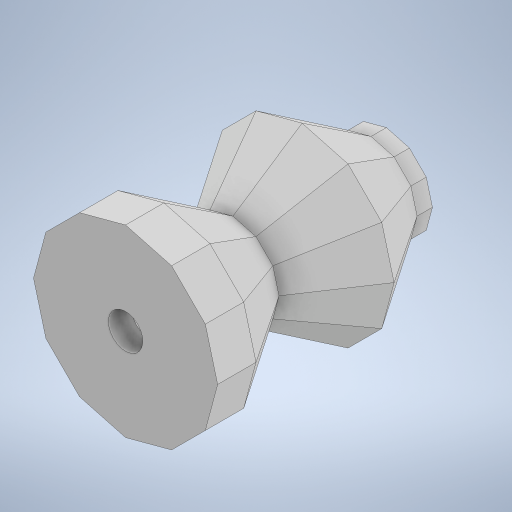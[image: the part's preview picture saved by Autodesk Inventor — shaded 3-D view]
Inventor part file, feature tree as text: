
AUTODESK INVENTOR PART (.ipt)
format: ipt  version: 2023 (Build 270158000, 158)  size: 359,424 bytes
history: native  units: in
note: dims shown in document units (in); Inventor stores cm internally (conversion verified against a paired STEP export)
features: sketch x6, extrude x4, projected_geometry x3, other x2, mirror x2, loft x1, shell x1
ambient origin geometry x8: Origin, YZ Plane, XZ Plane, XY Plane, X Axis, Y Axis, Z Axis, Center Point
bodies: Body1 (feature_tree)
feature tree (19):
  other  "솔리드1"
  sketch  "스케치1"
  other  "작업 평면1"
  loft  "로프트1"
  mirror  "미러1"
  mirror  "미러2"
  extrude  "돌출1"  Depth=0.3543in
  shell  "쉘5"  Thickness=0.4724in
  extrude  "돌출14"  TaperAngle=0.0deg  [1 undecoded]
  extrude  "돌출15"  TaperAngle=0.0deg  [1 undecoded]
  extrude  "돌출16"  Depth=0.1299in TaperAngle=0.0deg
  sketch  "스케치2"
  sketch  "스케치3"
  projected_geometry  "투영된 루프1"
  sketch  "스케치16"
  projected_geometry  "투영된 루프10"
  sketch  "스케치17"
  sketch  "스케치18"
  projected_geometry  "투영된 루프11"
note: 2 required parameter values undecoded (feature->parameter linkage not recoverable at this tier; creation-order binding heuristic only, values carry confidence <= 0.55)
